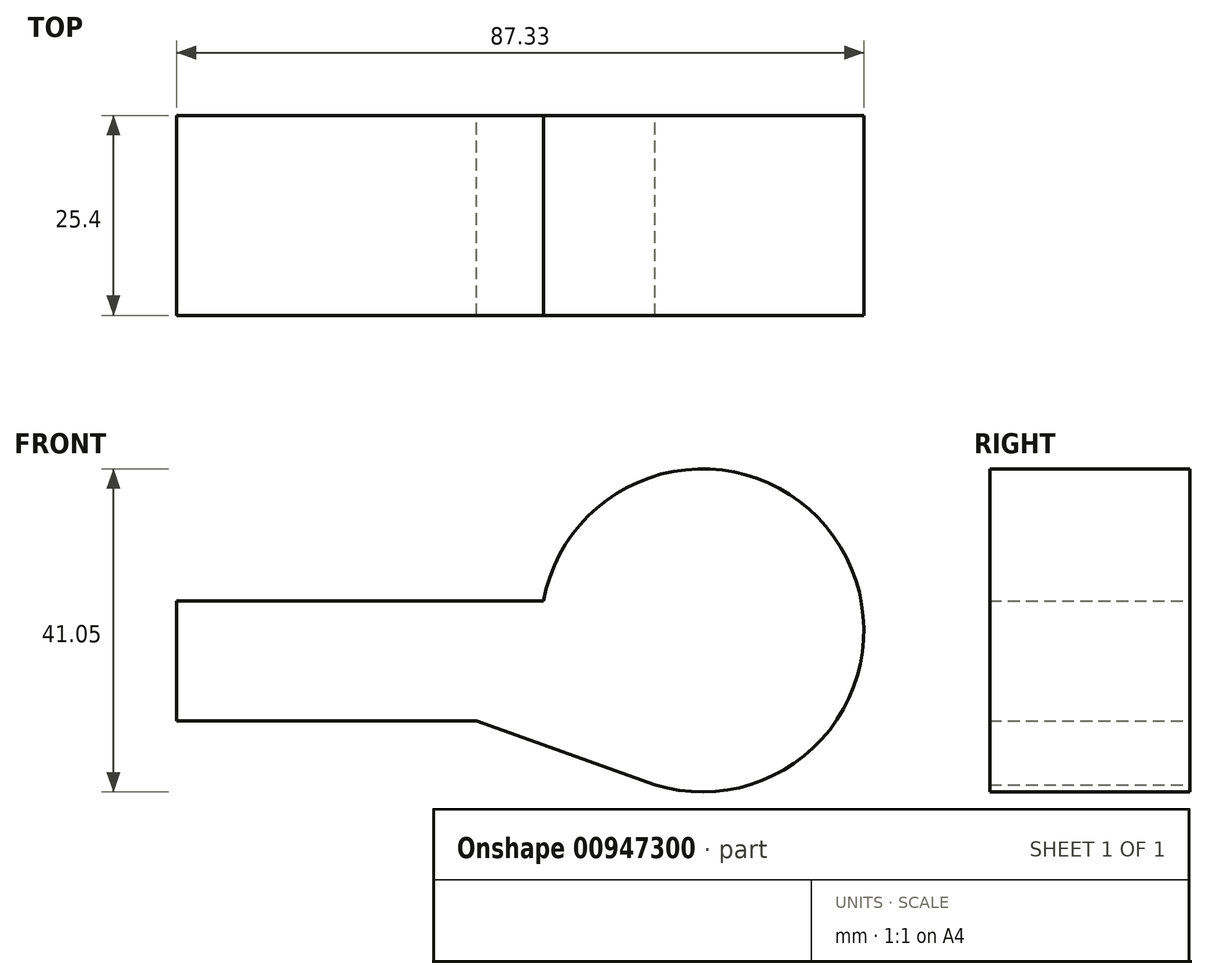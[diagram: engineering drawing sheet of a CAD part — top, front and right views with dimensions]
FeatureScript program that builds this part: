
annotation { "Feature Type Name" : "Feature", "Feature Type Description" : "" }
export const myFeature = defineFeature(function(context is Context, id is Id, definition is map)
    precondition{}
    {
        {
            var Q0;
            Q0=qCreatedBy(makeId("Front.planeOp"),FACE);
            var sketch = newSketch(context, id + "F0", { "sketchPlane" : qUnion([Q0])});
            skLineSegment(sketch, "E0", {"start": v(0, 0) * mm, "end": v(-38.1, 0) * mm});
            skLineSegment(sketch, "E1", {"start": v(-38.1, 0) * mm, "end": v(-38.1, -15.24) * mm});
            skLineSegment(sketch, "E2", {"start": v(-38.1, -15.24) * mm, "end": v(0, -15.24) * mm});
            skArc(sketch, "E3", {"start": v(20.88, -22.73) * mm, "mid": v(46.73, 6.05) * mm, "end": v(8.52, 0) * mm});
            skCircle(sketch, "E4", {"center": v(28.7, -3.75) * mm, "radius": 8.9 * mm});
            skLineSegment(sketch, "E5", {"start": v(0, 0) * mm, "end": v(23.6, -11.17) * mm});
            skLineSegment(sketch, "E6", {"start": v(0, -15.24) * mm, "end": v(22.68, -23.37) * mm});
            skLineSegment(sketch, "E7", {"start": v(0, 0) * mm, "end": v(8.52, 0) * mm});
            skSolve(sketch);
        }
        {
            var Q0;
            Q0=makeQuery(id+"F0.imprint","IMPRINT",FACE,{"disambiguationData":[TD([[makeQuery(id+"F0.imprint","IMPRINT",EDGE,{"derivedFrom":sQuery(id+"F0.wireOp",EDGE,"E0")}),1.0]])]});
            var Q1;
            Q1=makeQuery(id+"F0.imprint","IMPRINT",FACE,{"disambiguationData":[TD([[makeQuery(id+"F0.imprint","IMPRINT",EDGE,{"derivedFrom":sQuery(id+"F0.wireOp",EDGE,"E4")}),1.0]])]});
            extrude(context, id + "F1", {"entities" : qUnion([Q0, Q1]), "depth" : 25.4 * mm, "offsetDistance" : 25.4 * mm});
        }
    });
